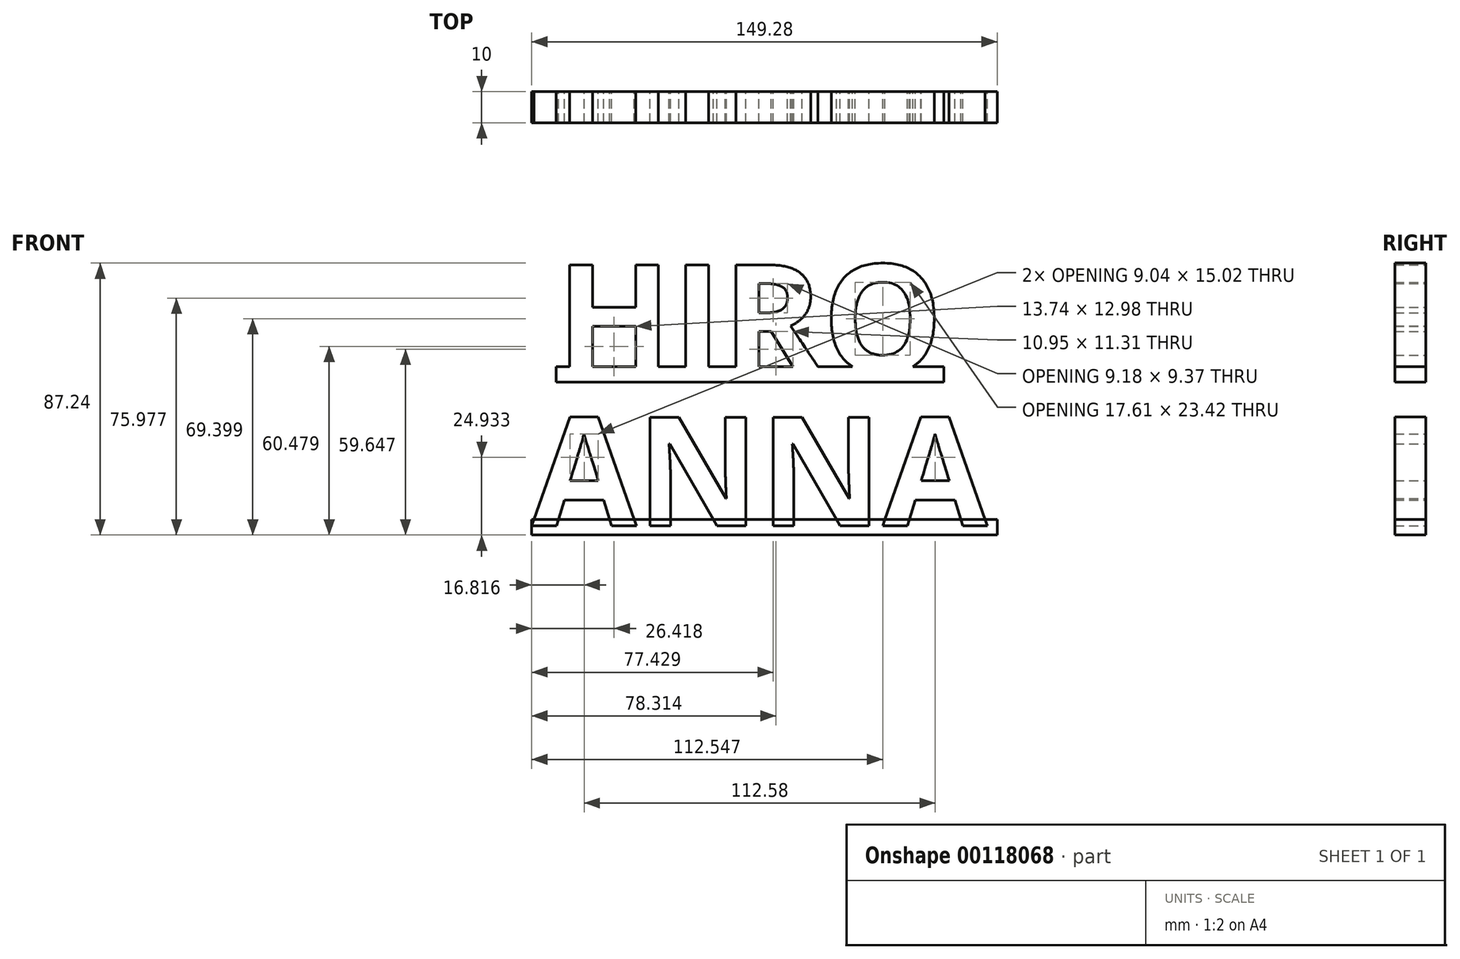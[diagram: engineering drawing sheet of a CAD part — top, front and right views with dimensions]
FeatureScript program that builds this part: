
annotation { "Feature Type Name" : "Feature", "Feature Type Description" : "" }
export const myFeature = defineFeature(function(context is Context, id is Id, definition is map)
    precondition{}
    {
        {
            var Q0;
            Q0=qCreatedBy(makeId("Front.planeOp"),FACE);
            var sketch = newSketch(context, id + "F0", { "sketchPlane" : qUnion([Q0])});
            skText(sketch, "E0", { "text": "HIRO", "fontName": "OpenSans-Bold.ttf"});
            skLineSegment(sketch, "E1.bottom", {"start": v(-49.94, 2) * mm, "end": v(74.46, 2) * mm});
            skLineSegment(sketch, "E1.top", {"start": v(-49.94, -3) * mm, "end": v(74.46, -3) * mm});
            skLineSegment(sketch, "E1.left", {"start": v(-49.94, 2) * mm, "end": v(-49.94, -3) * mm});
            skLineSegment(sketch, "E1.right", {"start": v(74.46, 2) * mm, "end": v(74.46, -3) * mm});
            const initialGuessF0  = {"E0": [-0.04994, 0, 1, 0, 0.035]};
            skSetInitialGuess(sketch, initialGuessF0);
            skSolve(sketch);
        }
        {
            var Q0;
            {var subQ8=sQuery(id+"F0.wireOp",EDGE,"E0.sketch_text.stroke-2");Q0=makeQuery(id+"F0.imprint","IMPRINT",FACE,{"disambiguationData":[TD([[makeQuery(id+"F0.imprint","IMPRINT",EDGE,{"derivedFrom":subQ8}),-1.0]])]});}
            var Q1;
            {var subQ0=sQuery(id+"F0.wireOp",EDGE,"E0.sketch_text.stroke-4");Q1=makeQuery(id+"F0.imprint","IMPRINT",FACE,{"disambiguationData":[TD([[makeQuery(id+"F0.imprint","IMPRINT",EDGE,{"derivedFrom":subQ0}),-1.0]])]});}
            var Q2;
            {var subQ21=sQuery(id+"F0.wireOp",EDGE,"E0.sketch_text.stroke-0");Q2=makeQuery(id+"F0.imprint","IMPRINT",FACE,{"disambiguationData":[TD([[makeQuery(id+"F0.imprint","IMPRINT",EDGE,{"derivedFrom":subQ21}),1.0]])]});}
            var Q3;
            {var subQ0=sQuery(id+"F0.wireOp",EDGE,"E0.sketch_text.stroke-0");Q3=makeQuery(id+"F0.imprint","IMPRINT",FACE,{"disambiguationData":[TD([[makeQuery(id+"F0.imprint","IMPRINT",EDGE,{"derivedFrom":subQ0}),-1.0]])]});}
            var Q4;
            {var subQ0=sQuery(id+"F0.wireOp",EDGE,"E0.sketch_text.stroke-13");Q4=makeQuery(id+"F0.imprint","IMPRINT",FACE,{"disambiguationData":[TD([[makeQuery(id+"F0.imprint","IMPRINT",EDGE,{"derivedFrom":subQ0}),-1.0]])]});}
            var Q5;
            {var subQ0=sQuery(id+"F0.wireOp",EDGE,"E0.sketch_text.stroke-15");Q5=makeQuery(id+"F0.imprint","IMPRINT",FACE,{"disambiguationData":[TD([[makeQuery(id+"F0.imprint","IMPRINT",EDGE,{"derivedFrom":subQ0}),-1.0]])]});}
            var Q6;
            Q6=makeQuery(id+"F0.imprint","IMPRINT",FACE,{"disambiguationData":[TD([[makeQuery(id+"F0.imprint","IMPRINT",EDGE,{"derivedFrom":sQuery(id+"F0.wireOp",EDGE,"E0.sketch_text.stroke-16")}),-1.0]])]});
            var Q7;
            {var subQ0=sQuery(id+"F0.wireOp",EDGE,"E0.sketch_text.stroke-24");Q7=makeQuery(id+"F0.imprint","IMPRINT",FACE,{"disambiguationData":[TD([[makeQuery(id+"F0.imprint","IMPRINT",EDGE,{"derivedFrom":subQ0}),-1.0]])]});}
            var Q8;
            {var subQ0=sQuery(id+"F0.wireOp",EDGE,"E0.sketch_text.stroke-32");Q8=makeQuery(id+"F0.imprint","IMPRINT",FACE,{"disambiguationData":[TD([[makeQuery(id+"F0.imprint","IMPRINT",EDGE,{"derivedFrom":subQ0}),-1.0]])]});}
            var Q9;
            {var subQ5=sQuery(id+"F0.wireOp",EDGE,"E0.sketch_text.stroke-35");Q9=makeQuery(id+"F0.imprint","IMPRINT",FACE,{"disambiguationData":[TD([[makeQuery(id+"F0.imprint","IMPRINT",EDGE,{"derivedFrom":subQ5}),-1.0]])]});}
            var Q10;
            {var subQ0=sQuery(id+"F0.wireOp",EDGE,"E0.sketch_text.stroke-37");var subQ1=sQuery(id+"F0.wireOp",EDGE,"E0.sketch_text.stroke-36");var subQ2=makeQuery(id+"F0.imprint","INTERSECT",VERTEX,{"derivedFrom":[subQ1,subQ0]});Q10=makeQuery(id+"F0.imprint","IMPRINT",FACE,{"disambiguationData":[TD([[makeQuery(id+"F0.imprint","IMPRINT",EDGE,{"disambiguationData":[TD([[subQ2,1.0]])],"derivedFrom":subQ1}),-1.0]])]});}
            extrude(context, id + "F1", {"entities" : qUnion([Q0, Q1, Q2, Q3, Q4, Q5, Q6, Q7, Q8, Q9, Q10]), "depth" : 10 * mm});
        }
        {
            var Q0;
            Q0=qCreatedBy(makeId("Front.planeOp"),FACE);
            var sketch = newSketch(context, id + "F2", { "sketchPlane" : qUnion([Q0])});
            skText(sketch, "E2", { "text": "ANNA", "fontName": "OpenSans-Bold.ttf"});
            skLineSegment(sketch, "E3.bottom", {"start": v(-57.76, -47) * mm, "end": v(91.52, -47) * mm});
            skLineSegment(sketch, "E3.top", {"start": v(-57.76, -52) * mm, "end": v(91.52, -52) * mm});
            skLineSegment(sketch, "E3.left", {"start": v(-57.76, -47) * mm, "end": v(-57.76, -52) * mm});
            skLineSegment(sketch, "E3.right", {"start": v(91.52, -47) * mm, "end": v(91.52, -52) * mm});
            const initialGuessF2  = {"E2": [-0.05776, -0.049, 1, 0, 0.035]};
            skSetInitialGuess(sketch, initialGuessF2);
            skSolve(sketch);
        }
        {
            var Q0;
            {var subQ4=sQuery(id+"F2.wireOp",EDGE,"E2.sketch_text.stroke-1");Q0=makeQuery(id+"F2.imprint","IMPRINT",FACE,{"disambiguationData":[TD([[makeQuery(id+"F2.imprint","IMPRINT",EDGE,{"derivedFrom":subQ4}),-1.0]])]});}
            var Q1;
            {var subQ0=sQuery(id+"F2.wireOp",EDGE,"E2.sketch_text.stroke-14");Q1=makeQuery(id+"F2.imprint","IMPRINT",FACE,{"disambiguationData":[TD([[makeQuery(id+"F2.imprint","IMPRINT",EDGE,{"derivedFrom":subQ0}),-1.0]])]});}
            var Q2;
            {var subQ7=sQuery(id+"F2.wireOp",EDGE,"E2.sketch_text.stroke-28");Q2=makeQuery(id+"F2.imprint","IMPRINT",FACE,{"disambiguationData":[TD([[makeQuery(id+"F2.imprint","IMPRINT",EDGE,{"derivedFrom":subQ7}),-1.0]])]});}
            var Q3;
            {var subQ0=sQuery(id+"F2.wireOp",EDGE,"E2.sketch_text.stroke-41");Q3=makeQuery(id+"F2.imprint","IMPRINT",FACE,{"disambiguationData":[TD([[makeQuery(id+"F2.imprint","IMPRINT",EDGE,{"derivedFrom":subQ0}),-1.0]])]});}
            var Q4;
            {var subQ0=sQuery(id+"F2.wireOp",EDGE,"E2.sketch_text.stroke-47");Q4=makeQuery(id+"F2.imprint","IMPRINT",FACE,{"disambiguationData":[TD([[makeQuery(id+"F2.imprint","IMPRINT",EDGE,{"derivedFrom":subQ0}),-1.0]])]});}
            var Q5;
            {var subQ15=sQuery(id+"F2.wireOp",EDGE,"E2.sketch_text.stroke-3");Q5=makeQuery(id+"F2.imprint","IMPRINT",FACE,{"disambiguationData":[TD([[makeQuery(id+"F2.imprint","IMPRINT",EDGE,{"derivedFrom":subQ15}),1.0]])]});}
            var Q6;
            {var subQ0=sQuery(id+"F2.wireOp",EDGE,"E2.sketch_text.stroke-43");Q6=makeQuery(id+"F2.imprint","IMPRINT",FACE,{"disambiguationData":[TD([[makeQuery(id+"F2.imprint","IMPRINT",EDGE,{"derivedFrom":subQ0}),-1.0]])]});}
            var Q7;
            {var subQ0=sQuery(id+"F2.wireOp",EDGE,"E2.sketch_text.stroke-26");Q7=makeQuery(id+"F2.imprint","IMPRINT",FACE,{"disambiguationData":[TD([[makeQuery(id+"F2.imprint","IMPRINT",EDGE,{"derivedFrom":subQ0}),-1.0]])]});}
            var Q8;
            {var subQ0=sQuery(id+"F2.wireOp",EDGE,"E2.sketch_text.stroke-31");Q8=makeQuery(id+"F2.imprint","IMPRINT",FACE,{"disambiguationData":[TD([[makeQuery(id+"F2.imprint","IMPRINT",EDGE,{"derivedFrom":subQ0}),-1.0]])]});}
            var Q9;
            {var subQ0=sQuery(id+"F2.wireOp",EDGE,"E2.sketch_text.stroke-12");Q9=makeQuery(id+"F2.imprint","IMPRINT",FACE,{"disambiguationData":[TD([[makeQuery(id+"F2.imprint","IMPRINT",EDGE,{"derivedFrom":subQ0}),-1.0]])]});}
            var Q10;
            {var subQ0=sQuery(id+"F2.wireOp",EDGE,"E2.sketch_text.stroke-17");Q10=makeQuery(id+"F2.imprint","IMPRINT",FACE,{"disambiguationData":[TD([[makeQuery(id+"F2.imprint","IMPRINT",EDGE,{"derivedFrom":subQ0}),-1.0]])]});}
            var Q11;
            {var subQ0=sQuery(id+"F2.wireOp",EDGE,"E2.sketch_text.stroke-7");Q11=makeQuery(id+"F2.imprint","IMPRINT",FACE,{"disambiguationData":[TD([[makeQuery(id+"F2.imprint","IMPRINT",EDGE,{"derivedFrom":subQ0}),-1.0]])]});}
            var Q12;
            {var subQ0=sQuery(id+"F2.wireOp",EDGE,"E2.sketch_text.stroke-3");Q12=makeQuery(id+"F2.imprint","IMPRINT",FACE,{"disambiguationData":[TD([[makeQuery(id+"F2.imprint","IMPRINT",EDGE,{"derivedFrom":subQ0}),-1.0]])]});}
            var Q13;
            {var subQ0=sQuery(id+"F2.wireOp",EDGE,"E3.left");var subQ3=sQuery(id+"F2.wireOp",EDGE,"E3.bottom");var subQ5=makeQuery(id+"F2.imprint","INTERSECT",VERTEX,{"derivedFrom":[subQ3,subQ0]});Q13=makeQuery(id+"F2.imprint","IMPRINT",FACE,{"disambiguationData":[TD([[makeQuery(id+"F2.imprint","IMPRINT",EDGE,{"disambiguationData":[TD([[subQ5,-1.0]])],"derivedFrom":subQ3}),-1.0]])]});}
            extrude(context, id + "F3", {"entities" : qUnion([Q0, Q1, Q2, Q3, Q4, Q5, Q6, Q7, Q8, Q9, Q10, Q11, Q12, Q13]), "depth" : 10 * mm});
        }
    });
